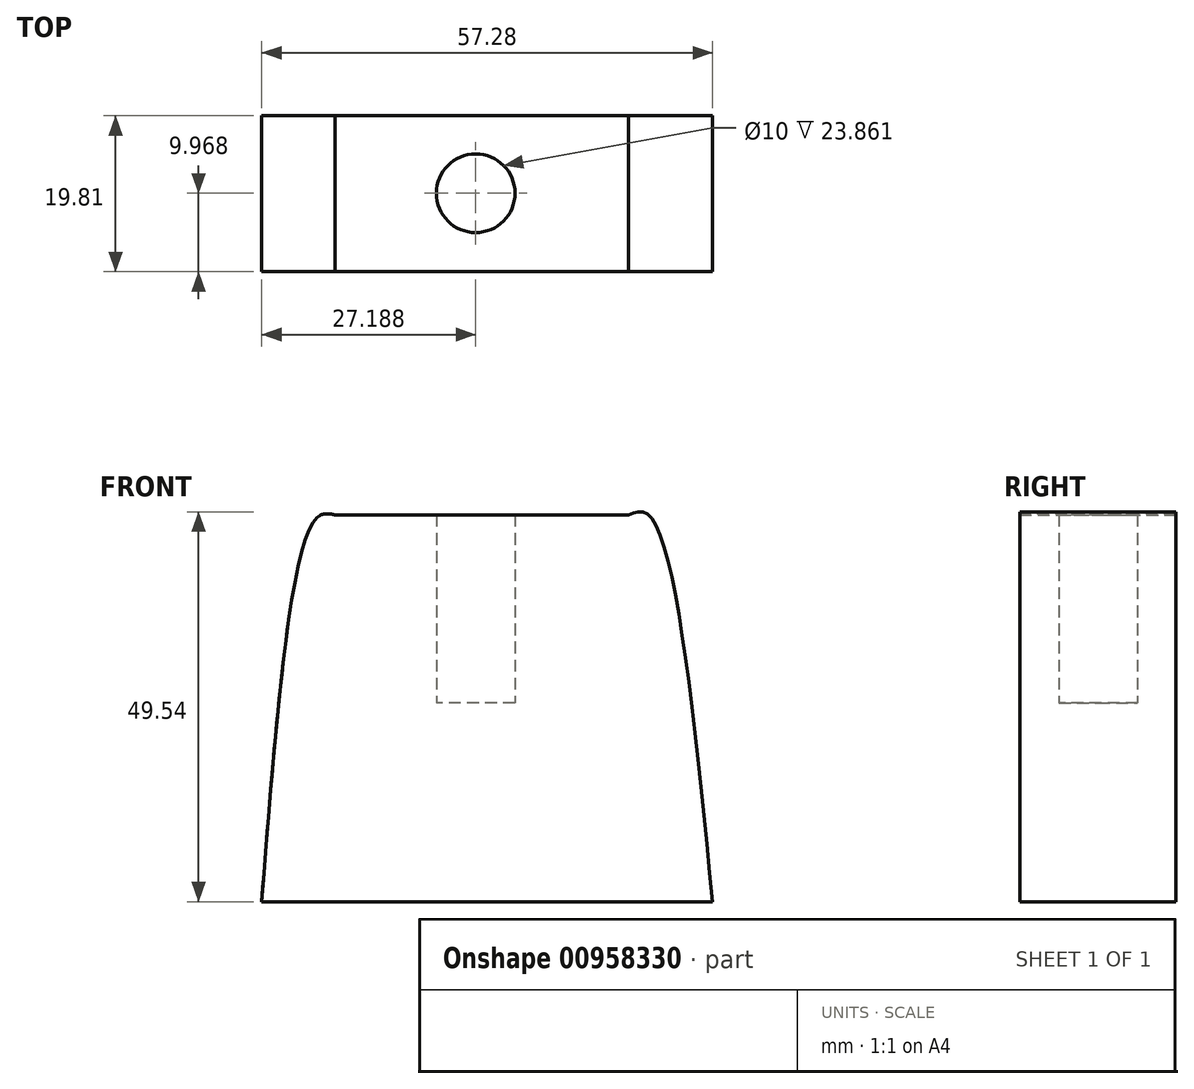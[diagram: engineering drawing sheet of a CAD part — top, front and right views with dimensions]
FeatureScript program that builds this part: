
annotation { "Feature Type Name" : "Feature", "Feature Type Description" : "" }
export const myFeature = defineFeature(function(context is Context, id is Id, definition is map)
    precondition{}
    {
        {
            var Q0;
            Q0=qCreatedBy(makeId("Front.planeOp"),FACE);
            var sketch = newSketch(context, id + "F0", { "sketchPlane" : qUnion([Q0])});
            skLineSegment(sketch, "E0", {"start": v(-57.28, -25.28) * mm, "end": v(0, -25.28) * mm});
            skFitSpline(sketch, "E1", {"points": [v(-57.28, -25.28) * mm, v(-50.34, 23.44) * mm, v(-47.94, 23.86) * mm], "startDerivative": vector(6.55, 82.98) * mm, "endDerivative": vector(13.64, -2.89) * mm});
            skLineSegment(sketch, "E2", {"start": v(-47.94, 23.86) * mm, "end": v(-10.7, 23.86) * mm});
            skFitSpline(sketch, "E3", {"points": [v(-10.7, 23.86) * mm, v(-8.14, 23.86) * mm, v(0, -25.28) * mm], "startDerivative": vector(14.17, 5.56) * mm, "endDerivative": vector(8.42, -84.82) * mm});
            skSolve(sketch);
        }
        {
            var Q0;
            Q0 = qSketchRegion(id + "F0", true);
            extrude(context, id + "F1", {"entities" : qUnion([Q0]), "depth" : 19.8 * mm, "offsetDistance" : 25.4 * mm});
        }
        {
            var Q0;
            Q0=qCreatedBy(makeId("Top.planeOp"),FACE);
            var sketch = newSketch(context, id + "F2", { "sketchPlane" : qUnion([Q0])});
            skCircle(sketch, "E4", {"center": v(-30.1, -9.84) * mm, "radius": 5 * mm});
            skSolve(sketch);
        }
        {
            var Q0;
            Q0 = qSketchRegion(id + "F2", true);
            extrude(context, id + "F3", {"entities" : qUnion([Q0]), "operationType" : NewBodyOperationType.REMOVE, "depth" : 29.97 * mm, "offsetDistance" : 25.4 * mm});
        }
    });
